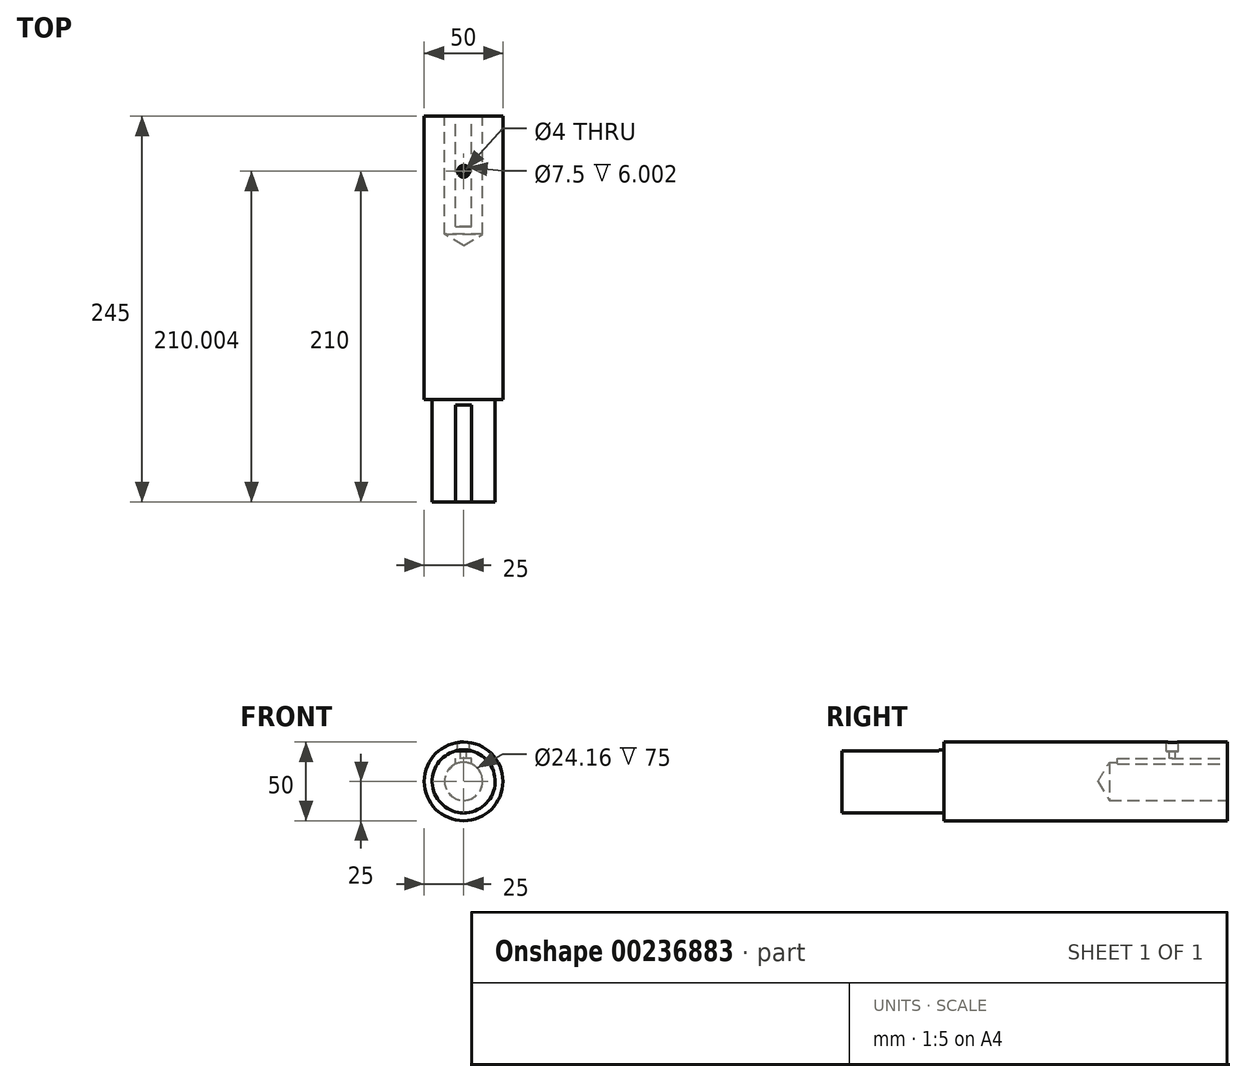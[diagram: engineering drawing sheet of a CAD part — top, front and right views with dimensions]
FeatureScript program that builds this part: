
annotation { "Feature Type Name" : "Feature", "Feature Type Description" : "" }
export const myFeature = defineFeature(function(context is Context, id is Id, definition is map)
    precondition{}
    {
        {
            var Q0;
            Q0=qCreatedBy(makeId("Front.planeOp"),FACE);
            var sketch = newSketch(context, id + "F0", { "sketchPlane" : qUnion([Q0])});
            skCircle(sketch, "E0", {"center": v(0, 0) * mm, "radius": 25 * mm});
            skSolve(sketch);
        }
        {
            var Q0;
            Q0 = qSketchRegion(id + "F0", true);
            extrude(context, id + "F1", {"entities" : qUnion([Q0]), "depth" : 180 * mm});
        }
        {
            var Q0;
            Q0=makeQuery(id+"F1.opExtrude","CAP_FACE",FACE,{"disambiguationData":[OSD([sQuery(id+"F0.wireOp",EDGE,"E0")])],"isStart":false});
            var sketch = newSketch(context, id + "F2", { "sketchPlane" : qUnion([Q0])});
            skCircle(sketch, "E1", {"center": v(0, 0) * mm, "radius": 20 * mm});
            skSolve(sketch);
        }
        {
            var Q0;
            Q0 = qSketchRegion(id + "F2", true);
            extrude(context, id + "F3", {"entities" : qUnion([Q0]), "operationType" : NewBodyOperationType.ADD, "depth" : 65 * mm});
        }
        {
            var Q0;
            Q0=makeQuery(id+"F3.opExtrude","CAP_FACE",FACE,{"disambiguationData":[OSD([sQuery(id+"F2.wireOp",EDGE,"E1")])],"isStart":false});
            var sketch = newSketch(context, id + "F4", { "sketchPlane" : qUnion([Q0])});
            skLineSegment(sketch, "E2.0", {"start": v(5, 19.36) * mm, "end": v(5, 22.56) * mm});
            skLineSegment(sketch, "E3", {"start": v(5, 19.36) * mm, "end": v(-5, 19.36) * mm});
            skLineSegment(sketch, "E4", {"start": v(-5, 19.36) * mm, "end": v(-5, 22.56) * mm});
            skLineSegment(sketch, "E5", {"start": v(-5, 22.56) * mm, "end": v(5, 22.56) * mm});
            skPoint(sketch, "E6.start.orphan", {"position": v(0, 0) * mm});
            skSolve(sketch);
        }
        {
            var Q0;
            Q0 = qSketchRegion(id + "F4", true);
            extrude(context, id + "F5", {"entities" : qUnion([Q0]), "operationType" : NewBodyOperationType.REMOVE, "oppositeDirection" : true, "depth" : 61.7 * mm});
        }
        {
            var Q0;
            Q0=makeQuery(id+"F1.opExtrude","CAP_FACE",FACE,{"disambiguationData":[OSD([sQuery(id+"F0.wireOp",EDGE,"E0")])],"isStart":true});
            var sketch = newSketch(context, id + "F6", { "sketchPlane" : qUnion([Q0])});
            skPoint(sketch, "E7", {"position": v(0, 0) * mm});
            skSolve(sketch);
        }
        {
            var Q0;
            Q0=sQuery(id+"F6.wireOp",VERTEX,"E7");
            var Q1;
            Q1=makeQuery(id+"F1.opExtrude","SWEPT_BODY",BODY,{"disambiguationData":[OSD([sQuery(id+"F0.wireOp",EDGE,"E0")])]});
            hole(context, id + "F7", {"style" : HoleStyle.SIMPLE, "endStyle" : HoleEndStyle.BLIND, "holeDiameter" : 24.16 * mm, "holeDepth" : 75 * mm, "locations" : qUnion([Q0]), "scope" : qUnion([Q1])});
        }
        {
            var Q0;
            Q0=makeQuery(id+"F1.opExtrude","CAP_FACE",FACE,{"disambiguationData":[OSD([sQuery(id+"F0.wireOp",EDGE,"E0")])],"isStart":true});
            var sketch = newSketch(context, id + "F8", { "sketchPlane" : qUnion([Q0])});
            skLineSegment(sketch, "E8.0", {"start": v(-5, 8.84) * mm, "end": v(-5, 14.5) * mm});
            skLineSegment(sketch, "E9.0", {"start": v(5, 8.84) * mm, "end": v(5, 14.5) * mm});
            skLineSegment(sketch, "E10", {"start": v(-5, 14.5) * mm, "end": v(5, 14.5) * mm});
            skLineSegment(sketch, "E11", {"start": v(-5, 8.84) * mm, "end": v(5, 8.84) * mm});
            skPoint(sketch, "E12.orphan", {"position": v(0, 0) * mm});
            skSolve(sketch);
        }
        {
            var Q0;
            Q0 = qSketchRegion(id + "F8", true);
            extrude(context, id + "F9", {"entities" : qUnion([Q0]), "operationType" : NewBodyOperationType.REMOVE, "oppositeDirection" : true, "depth" : 70 * mm});
        }
        {
            var Q0;
            Q0=qCreatedBy(makeId("Top.planeOp"),FACE);
            cPlane(context, id + "F10", {"entities" : qUnion([Q0]), "cplaneType" : CPlaneType.OFFSET, "offset" : 25 * mm, "width" : 150 * mm, "height" : 150 * mm});
        }
        {
            var Q0;
            Q0=qCreatedBy(id+"F10.planeOp",FACE);
            var sketch = newSketch(context, id + "F11", { "sketchPlane" : qUnion([Q0])});
            skCircle(sketch, "E13", {"center": v(0, -35) * mm, "radius": 2 * mm});
            skSolve(sketch);
        }
        {
            var Q0;
            Q0 = qSketchRegion(id + "F11", true);
            extrude(context, id + "F12", {"entities" : qUnion([Q0]), "operationType" : NewBodyOperationType.REMOVE, "oppositeDirection" : true, "depth" : 25 * mm});
        }
        {
            var Q0;
            Q0=qCreatedBy(id+"F10.planeOp",FACE);
            var sketch = newSketch(context, id + "F13", { "sketchPlane" : qUnion([Q0])});
            skCircle(sketch, "E14", {"center": v(0, -35) * mm, "radius": 3.75 * mm});
            skSolve(sketch);
        }
        {
            var Q0;
            Q0 = qSketchRegion(id + "F13", true);
            extrude(context, id + "F14", {"entities" : qUnion([Q0]), "operationType" : NewBodyOperationType.REMOVE, "oppositeDirection" : true, "depth" : 6 * mm});
        }
    });
